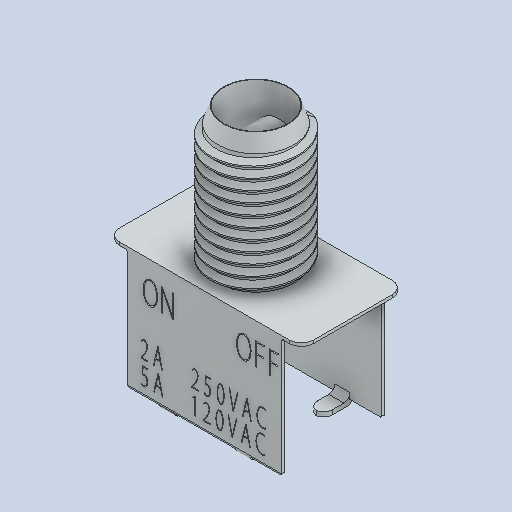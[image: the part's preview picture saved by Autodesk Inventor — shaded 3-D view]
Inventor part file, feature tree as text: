
AUTODESK INVENTOR PART (.ipt)
format: ipt  version: 2025.1 (Build 291241020, 241B)  size: 976,384 bytes
history: native  units: in
note: dims shown in document units (in); Inventor stores cm internally (conversion verified against a paired STEP export)
features: other x2, mirror x1, fillet x1
ambient origin geometry x8: Origin, YZ Plane, XZ Plane, XY Plane, X Axis, Y Axis, Z Axis, Center Point
bodies: Solid1 (feature_tree)
feature tree (4):
  mirror  "MirrorPlane"
  other  "Plane1"
  other  "Plane2"
  fillet  "Fillet5"  [1 undecoded]
note: 1 required parameter value undecoded (feature->parameter linkage not recoverable at this tier; creation-order binding heuristic only, values carry confidence <= 0.55)
